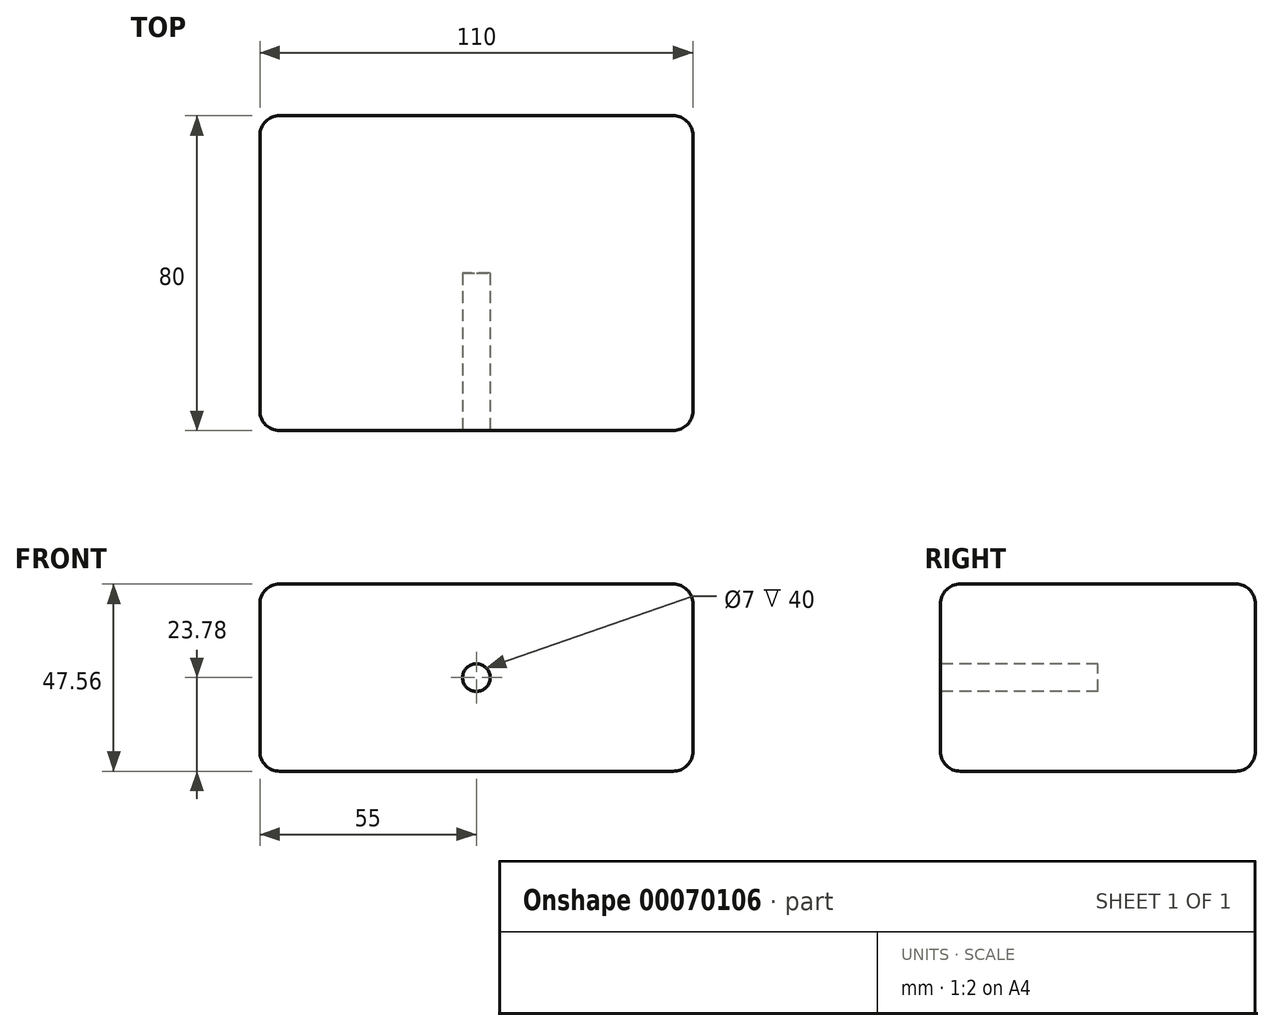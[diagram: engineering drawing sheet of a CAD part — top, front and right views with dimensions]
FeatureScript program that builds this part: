
annotation { "Feature Type Name" : "Feature", "Feature Type Description" : "" }
export const myFeature = defineFeature(function(context is Context, id is Id, definition is map)
    precondition{}
    {
        {
            var Q0;
            Q0=qCreatedBy(makeId("Front.planeOp"),FACE);
            var sketch = newSketch(context, id + "F0", { "sketchPlane" : qUnion([Q0])});
            skLineSegment(sketch, "E0.rect.bottom", {"start": v(55, 23.78) * mm, "end": v(-55, 23.78) * mm});
            skLineSegment(sketch, "E0.rect.top", {"start": v(55, -23.78) * mm, "end": v(-55, -23.78) * mm});
            skLineSegment(sketch, "E0.rect.left", {"start": v(55, 23.78) * mm, "end": v(55, -23.78) * mm});
            skLineSegment(sketch, "E0.rect.right", {"start": v(-55, 23.78) * mm, "end": v(-55, -23.78) * mm});
            skPoint(sketch, "E0.rect.middle", {"position": v(0, 0) * mm});
            skSolve(sketch);
        }
        {
            var Q0;
            Q0=makeQuery(id+"F0.imprint","IMPRINT",FACE,{"disambiguationData":[TD([[makeQuery(id+"F0.imprint","IMPRINT",EDGE,{"derivedFrom":sQuery(id+"F0.wireOp",EDGE,"E0.rect.bottom")}),1.0]])]});
            extrude(context, id + "F1", {"entities" : qUnion([Q0]), "depth" : 80 * mm});
        }
        {
            var Q0;
            Q0=makeQuery(id+"F1.opExtrude","CAP_FACE",FACE,{"disambiguationData":[OSD([sQuery(id+"F0.wireOp",EDGE,"E0.rect.bottom"),sQuery(id+"F0.wireOp",EDGE,"E0.rect.top"),sQuery(id+"F0.wireOp",EDGE,"E0.rect.left"),sQuery(id+"F0.wireOp",EDGE,"E0.rect.right")])],"isStart":false});
            var sketch = newSketch(context, id + "F2", { "sketchPlane" : qUnion([Q0])});
            skCircle(sketch, "E1", {"center": v(0, 0) * mm, "radius": 3.5 * mm});
            skSolve(sketch);
        }
        {
            var Q0;
            Q0=makeQuery(id+"F2.imprint","IMPRINT",FACE,{"disambiguationData":[TD([[makeQuery(id+"F2.imprint","IMPRINT",EDGE,{"derivedFrom":sQuery(id+"F2.wireOp",EDGE,"E1")}),1.0]])]});
            extrude(context, id + "F3", {"entities" : qUnion([Q0]), "operationType" : NewBodyOperationType.REMOVE, "oppositeDirection" : true, "depth" : 40 * mm});
        }
        {
            var Q0;
            Q0=makeQuery(id+"F1.opExtrude","CAP_EDGE",EDGE,{"disambiguationData":[OSD([sQuery(id+"F0.wireOp",EDGE,"E0.rect.bottom")])],"isStart":false});
            var Q1;
            Q1=makeQuery(id+"F1.opExtrude","CAP_EDGE",EDGE,{"disambiguationData":[OSD([sQuery(id+"F0.wireOp",EDGE,"E0.rect.right")])],"isStart":false});
            var Q2;
            Q2=makeQuery(id+"F1.opExtrude","CAP_EDGE",EDGE,{"disambiguationData":[OSD([sQuery(id+"F0.wireOp",EDGE,"E0.rect.top")])],"isStart":false});
            var Q3;
            Q3=makeQuery(id+"F1.opExtrude","CAP_EDGE",EDGE,{"disambiguationData":[OSD([sQuery(id+"F0.wireOp",EDGE,"E0.rect.left")])],"isStart":false});
            var Q4;
            Q4=makeQuery(id+"F1.opExtrude","SWEPT_EDGE",EDGE,{"disambiguationData":[OSD([sQuery(id+"F0.wireOp",EDGE,"E0.rect.bottom"),sQuery(id+"F0.wireOp",EDGE,"E0.rect.right")])]});
            var Q5;
            Q5=makeQuery(id+"F1.opExtrude","CAP_EDGE",EDGE,{"disambiguationData":[OSD([sQuery(id+"F0.wireOp",EDGE,"E0.rect.bottom")])],"isStart":true});
            var Q6;
            Q6=makeQuery(id+"F1.opExtrude","SWEPT_EDGE",EDGE,{"disambiguationData":[OSD([sQuery(id+"F0.wireOp",EDGE,"E0.rect.bottom"),sQuery(id+"F0.wireOp",EDGE,"E0.rect.left")])]});
            var Q7;
            Q7=makeQuery(id+"F1.opExtrude","SWEPT_EDGE",EDGE,{"disambiguationData":[OSD([sQuery(id+"F0.wireOp",EDGE,"E0.rect.top"),sQuery(id+"F0.wireOp",EDGE,"E0.rect.left")])]});
            var Q8;
            Q8=makeQuery(id+"F1.opExtrude","SWEPT_EDGE",EDGE,{"disambiguationData":[OSD([sQuery(id+"F0.wireOp",EDGE,"E0.rect.top"),sQuery(id+"F0.wireOp",EDGE,"E0.rect.right")])]});
            var Q9;
            Q9=makeQuery(id+"F1.opExtrude","CAP_EDGE",EDGE,{"disambiguationData":[OSD([sQuery(id+"F0.wireOp",EDGE,"E0.rect.top")])],"isStart":true});
            var Q10;
            Q10=makeQuery(id+"F1.opExtrude","CAP_EDGE",EDGE,{"disambiguationData":[OSD([sQuery(id+"F0.wireOp",EDGE,"E0.rect.left")])],"isStart":true});
            var Q11;
            Q11=makeQuery(id+"F1.opExtrude","CAP_EDGE",EDGE,{"disambiguationData":[OSD([sQuery(id+"F0.wireOp",EDGE,"E0.rect.right")])],"isStart":true});
            var Q12;
            Q12=makeQuery(id+"F3.boolean.opBoolean","COPY",EDGE,{"derivedFrom":makeQuery(id+"F3.opExtrude","CAP_EDGE",EDGE,{"disambiguationData":[OSD([sQuery(id+"F2.wireOp",EDGE,"E1")])],"isStart":true})});
            fillet(context, id + "F4", {"entities" : qUnion([Q0, Q1, Q2, Q3, Q4, Q5, Q6, Q7, Q8, Q9, Q10, Q11, Q12]), "radius" : 5 * mm, "tangentPropagation" : true, "allowEdgeOverflow" : false});
        }
    });
